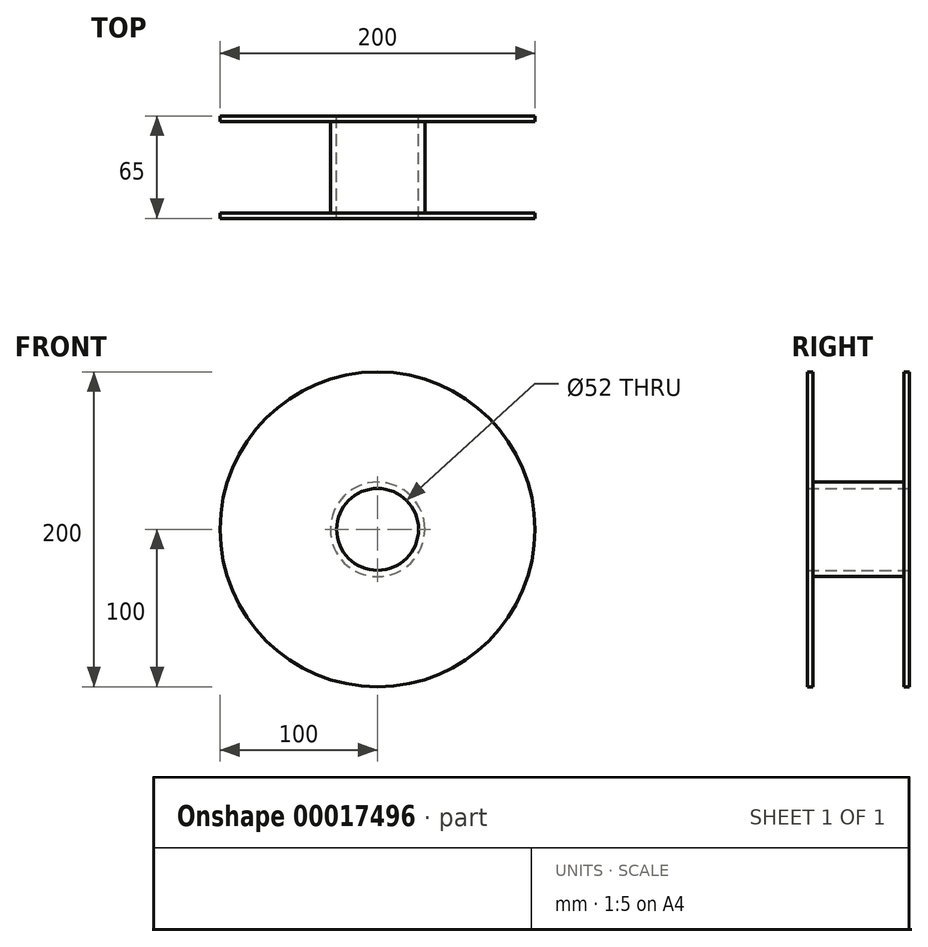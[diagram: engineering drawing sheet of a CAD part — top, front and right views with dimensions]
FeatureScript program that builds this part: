
annotation { "Feature Type Name" : "Feature", "Feature Type Description" : "" }
export const myFeature = defineFeature(function(context is Context, id is Id, definition is map)
    precondition{}
    {
        {
            var Q0;
            Q0=qCreatedBy(makeId("Front.planeOp"),FACE);
            var sketch = newSketch(context, id + "F0", { "sketchPlane" : qUnion([Q0])});
            skCircle(sketch, "E0", {"center": v(0, 0) * mm, "radius": 100 * mm});
            skCircle(sketch, "E1", {"center": v(0, 0) * mm, "radius": 26 * mm});
            skSolve(sketch);
        }
        {
            var Q0;
            Q0 = qSketchRegion(id + "F0", true);
            extrude(context, id + "F1", {"entities" : qUnion([Q0]), "endBound" : BoundingType.SYMMETRIC, "depth" : 65 * mm});
        }
        {
            var Q0;
            Q0=qCreatedBy(makeId("Top.planeOp"),FACE);
            var sketch = newSketch(context, id + "F2", { "sketchPlane" : qUnion([Q0])});
            skLineSegment(sketch, "E2", {"start": v(0, 0) * mm, "end": v(0, 21.03) * mm, "construction": true});
            skLineSegment(sketch, "E3.bottom", {"start": v(30, 29) * mm, "end": v(130, 29) * mm});
            skLineSegment(sketch, "E3.top", {"start": v(30, -29) * mm, "end": v(130, -29) * mm});
            skLineSegment(sketch, "E3.left", {"start": v(30, 29) * mm, "end": v(30, -29) * mm});
            skLineSegment(sketch, "E3.right", {"start": v(130, 29) * mm, "end": v(130, -29) * mm});
            skLineSegment(sketch, "E4", {"start": v(0, 0) * mm, "end": v(41.92, 0) * mm, "construction": true});
            skSolve(sketch);
        }
        {
            var Q0;
            Q0 = qSketchRegion(id + "F2", true);
            var Q1;
            Q1=sQuery(id+"F2.wireOp",EDGE,"E2");
            revolve(context, id + "F3", {"operationType" : NewBodyOperationType.REMOVE, "entities" : qUnion([Q0]), "axis" : qUnion([Q1]), "revolveType" : RevolveType.FULL, "oppositeDirection" : true});
        }
    });
